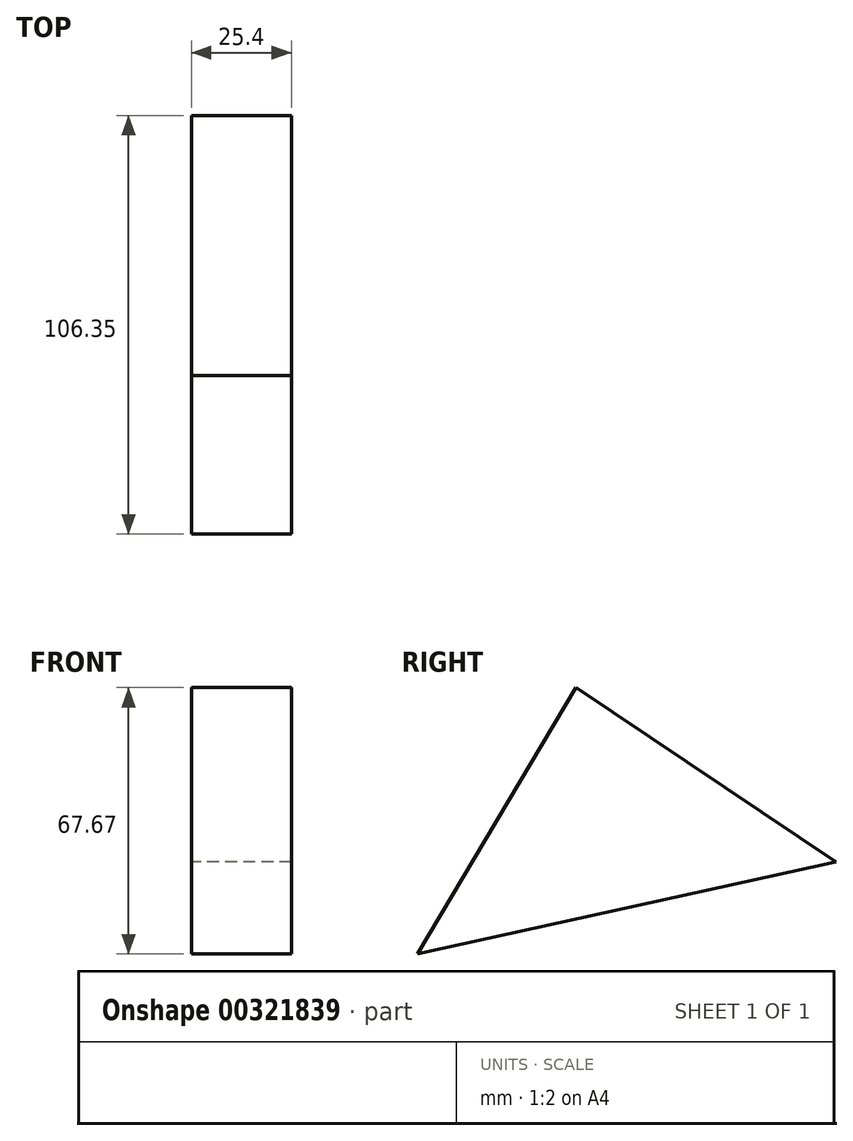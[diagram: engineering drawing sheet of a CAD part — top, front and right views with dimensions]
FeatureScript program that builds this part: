
annotation { "Feature Type Name" : "Feature", "Feature Type Description" : "" }
export const myFeature = defineFeature(function(context is Context, id is Id, definition is map)
    precondition{}
    {
        {
            var Q0;
            Q0=qCreatedBy(makeId("Right.planeOp"),FACE);
            var sketch = newSketch(context, id + "F0", { "sketchPlane" : qUnion([Q0])});
            skLineSegment(sketch, "E0", {"start": v(-129.04, 100.5) * mm, "end": v(-88.8, 168.16) * mm});
            skLineSegment(sketch, "E1", {"start": v(-88.8, 168.16) * mm, "end": v(-22.7, 123.88) * mm});
            skLineSegment(sketch, "E2", {"start": v(-22.7, 123.88) * mm, "end": v(-129.04, 100.5) * mm});
            skLineSegment(sketch, "E3", {"start": v(-55.74, 146.02) * mm, "end": v(-88.8, 168.16) * mm});
            skSolve(sketch);
        }
        {
            var Q0;
            Q0=makeQuery(id+"F0.imprint","IMPRINT",FACE,{"disambiguationData":[TD([[makeQuery(id+"F0.imprint","IMPRINT",EDGE,{"derivedFrom":sQuery(id+"F0.wireOp",EDGE,"E0")}),-1.0]])]});
            extrude(context, id + "F1", {"entities" : qUnion([Q0]), "depth" : 25.4 * mm});
        }
    });
